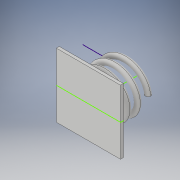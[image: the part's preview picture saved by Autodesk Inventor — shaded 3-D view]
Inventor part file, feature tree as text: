
AUTODESK INVENTOR PART (.ipt)
format: ipt  version: 2019 (Build 230136000, 136)  size: 417,792 bytes
history: native  units: mm
features: sketch x1, helix x1, extrude x1
ambient origin geometry x8: Origin, YZ Plane, XZ Plane, XY Plane, X Axis, Y Axis, Z Axis, Center Point
bodies: Solid1 (feature_tree)
feature tree (3):
  sketch  "Sketch1"  dims[d1=4.0mm d6=2.0mm d7=3.0mm d8=30.0mm d9=0.174533mm d10=90.0deg d11=90.0deg d12=0.0mm d13=0.0mm d15=6.0mm d16=0.0mm d18=3.0mm d20=3.0mm d21=2.0mm]
  helix  "Coil1"  [1 undecoded]
  extrude  "Extrusion1"  Depth=6.0mm TaperAngle=0.0deg
note: 1 required parameter value undecoded (feature->parameter linkage not recoverable at this tier; creation-order binding heuristic only, values carry confidence <= 0.55)
